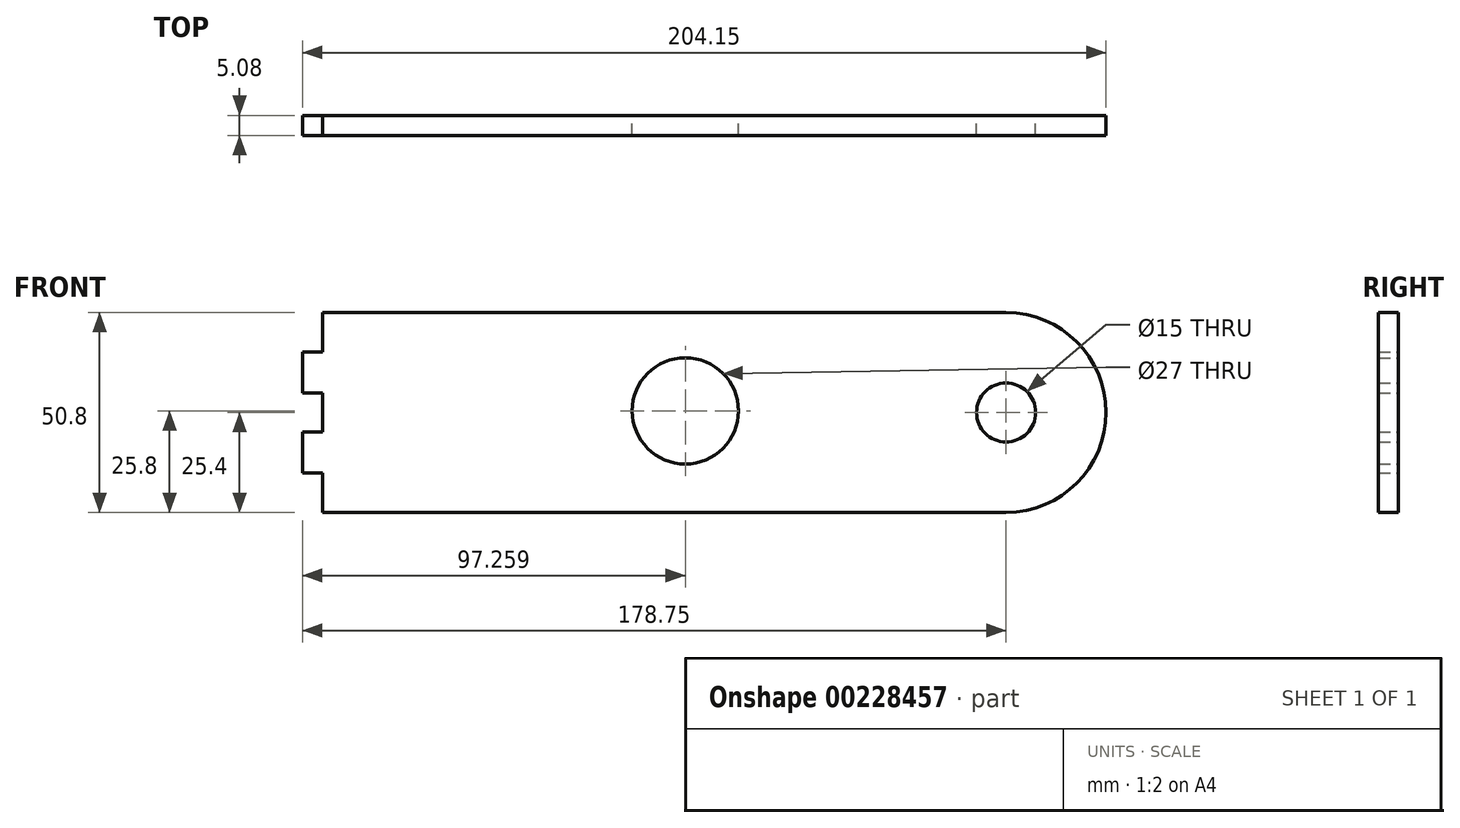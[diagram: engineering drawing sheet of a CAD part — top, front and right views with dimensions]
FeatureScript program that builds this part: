
annotation { "Feature Type Name" : "Feature", "Feature Type Description" : "" }
export const myFeature = defineFeature(function(context is Context, id is Id, definition is map)
    precondition{}
    {
        {
            var Q0;
            Q0=qCreatedBy(makeId("Front.planeOp"),FACE);
            var sketch = newSketch(context, id + "F0", { "sketchPlane" : qUnion([Q0])});
            skArc(sketch, "E0", {"start": v(178.75, 0) * mm, "mid": v(204.15, 25.4) * mm, "end": v(178.75, 50.8) * mm});
            skCircle(sketch, "E1", {"center": v(178.75, 25.4) * mm, "radius": 7.5 * mm});
            skCircle(sketch, "E2", {"center": v(97.26, 25.8) * mm, "radius": 13.5 * mm});
            skLineSegment(sketch, "E3", {"start": v(0, 50.8) * mm, "end": v(0, 0) * mm});
            skLineSegment(sketch, "E4", {"start": v(0, 50.8) * mm, "end": v(178.75, 50.8) * mm});
            skLineSegment(sketch, "E5", {"start": v(0, 0) * mm, "end": v(178.75, 0) * mm});
            skLineSegment(sketch, "E6.bottom", {"start": v(0, 40.8) * mm, "end": v(5.08, 40.8) * mm});
            skLineSegment(sketch, "E6.top", {"start": v(0, 50.8) * mm, "end": v(5.08, 50.8) * mm});
            skLineSegment(sketch, "E6.left", {"start": v(0, 40.8) * mm, "end": v(0, 50.8) * mm});
            skLineSegment(sketch, "E6.right", {"start": v(5.08, 40.8) * mm, "end": v(5.08, 50.8) * mm});
            skLineSegment(sketch, "E7.bottom", {"start": v(0, 30.4) * mm, "end": v(5.08, 30.4) * mm});
            skLineSegment(sketch, "E7.top", {"start": v(0, 20.4) * mm, "end": v(5.08, 20.4) * mm});
            skLineSegment(sketch, "E7.left", {"start": v(0, 30.4) * mm, "end": v(0, 20.4) * mm});
            skLineSegment(sketch, "E7.right", {"start": v(5.08, 30.4) * mm, "end": v(5.08, 20.4) * mm});
            skLineSegment(sketch, "E8.bottom", {"start": v(0, 0) * mm, "end": v(5.08, 0) * mm});
            skLineSegment(sketch, "E8.top", {"start": v(0, 10) * mm, "end": v(5.08, 10) * mm});
            skLineSegment(sketch, "E8.left", {"start": v(0, 0) * mm, "end": v(0, 10) * mm});
            skLineSegment(sketch, "E8.right", {"start": v(5.08, 0) * mm, "end": v(5.08, 10) * mm});
            skSolve(sketch);
        }
        {
            var Q0;
            Q0=makeQuery(id+"F0.imprint","IMPRINT",FACE,{"disambiguationData":[TD([[makeQuery(id+"F0.imprint","IMPRINT",EDGE,{"derivedFrom":sQuery(id+"F0.wireOp",EDGE,"E0")}),1.0]])]});
            extrude(context, id + "F1", {"entities" : qUnion([Q0]), "depth" : 5.08 * mm});
        }
    });
